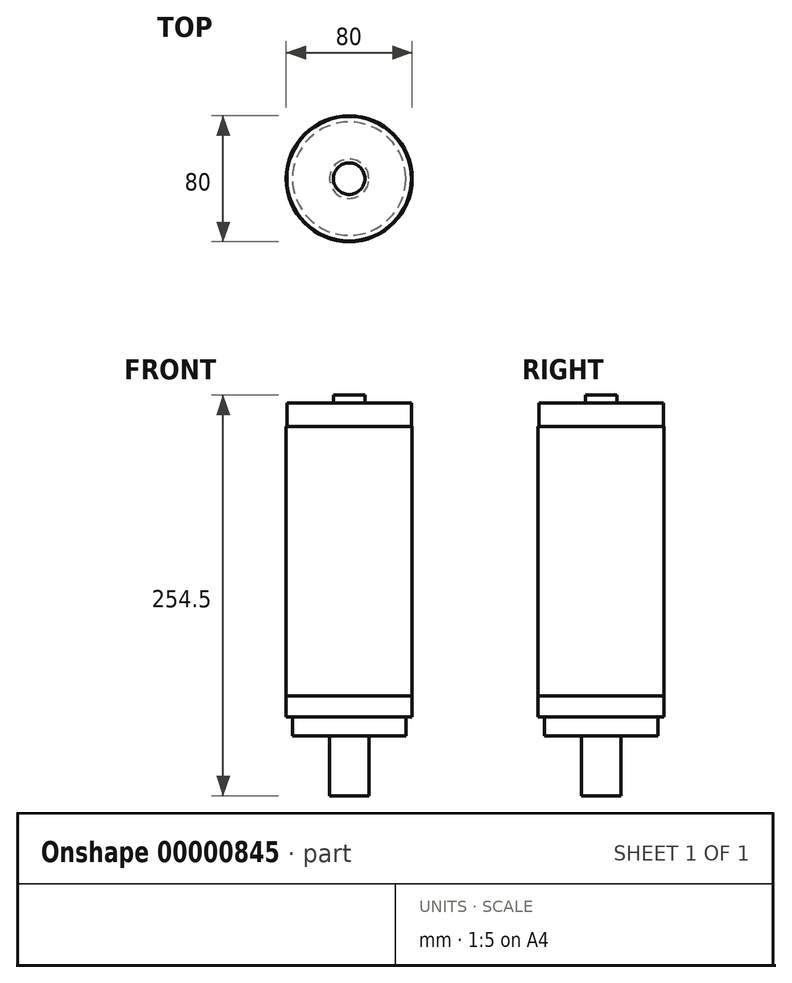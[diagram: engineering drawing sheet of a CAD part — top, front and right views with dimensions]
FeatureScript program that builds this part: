
annotation { "Feature Type Name" : "Feature", "Feature Type Description" : "" }
export const myFeature = defineFeature(function(context is Context, id is Id, definition is map)
    precondition{}
    {
        {
            var Q0;
            Q0=qCreatedBy(makeId("Top.planeOp"),FACE);
            var sketch = newSketch(context, id + "F0", { "sketchPlane" : qUnion([Q0])});
            skCircle(sketch, "E0", {"center": v(0, 0) * mm, "radius": 39.5 * mm});
            skSolve(sketch);
        }
        {
            var Q0;
            Q0=makeQuery(id+"F0.imprint","IMPRINT",FACE,{"disambiguationData":[TD([[makeQuery(id+"F0.imprint","IMPRINT",EDGE,{"derivedFrom":sQuery(id+"F0.wireOp",EDGE,"E0")}),1.0]])]});
            extrude(context, id + "F1", {"entities" : qUnion([Q0]), "oppositeDirection" : true, "depth" : 15 * mm});
        }
        {
            var Q0;
            Q0=makeQuery(id+"F1.opExtrude","CAP_FACE",FACE,{"disambiguationData":[OSD([sQuery(id+"F0.wireOp",EDGE,"E0")])],"isStart":false});
            var sketch = newSketch(context, id + "F2", { "sketchPlane" : qUnion([Q0])});
            skCircle(sketch, "E1", {"center": v(0, 0) * mm, "radius": 40 * mm});
            skSolve(sketch);
        }
        {
            var Q0;
            Q0 = qSketchRegion(id + "F2", true);
            extrude(context, id + "F3", {"entities" : qUnion([Q0]), "operationType" : NewBodyOperationType.ADD, "depth" : 171 * mm});
        }
        {
            var Q0;
            Q0=makeQuery(id+"F3.opExtrude","CAP_FACE",FACE,{"disambiguationData":[OSD([sQuery(id+"F2.wireOp",EDGE,"E1")])],"isStart":false});
            var sketch = newSketch(context, id + "F4", { "sketchPlane" : qUnion([Q0])});
            skCircle(sketch, "E2", {"center": v(0, 0) * mm, "radius": 39.95 * mm});
            skSolve(sketch);
        }
        {
            var Q0;
            Q0 = qSketchRegion(id + "F4", true);
            extrude(context, id + "F5", {"entities" : qUnion([Q0]), "operationType" : NewBodyOperationType.ADD, "depth" : 13.5 * mm});
        }
        {
            var Q0;
            Q0=makeQuery(id+"F5.opExtrude","CAP_FACE",FACE,{"disambiguationData":[OSD([sQuery(id+"F4.wireOp",EDGE,"E2")])],"isStart":false});
            var sketch = newSketch(context, id + "F6", { "sketchPlane" : qUnion([Q0])});
            skCircle(sketch, "E3", {"center": v(0, 0) * mm, "radius": 36 * mm});
            skSolve(sketch);
        }
        {
            var Q0;
            Q0 = qSketchRegion(id + "F6", true);
            extrude(context, id + "F7", {"entities" : qUnion([Q0]), "operationType" : NewBodyOperationType.ADD, "depth" : 12 * mm});
        }
        {
            var Q0;
            Q0=makeQuery(id+"F7.opExtrude","CAP_FACE",FACE,{"disambiguationData":[OSD([sQuery(id+"F6.wireOp",EDGE,"E3")])],"isStart":false});
            var sketch = newSketch(context, id + "F8", { "sketchPlane" : qUnion([Q0])});
            skCircle(sketch, "E4", {"center": v(0, 0) * mm, "radius": 12.5 * mm});
            skSolve(sketch);
        }
        {
            var Q0;
            Q0 = qSketchRegion(id + "F8", true);
            extrude(context, id + "F9", {"entities" : qUnion([Q0]), "operationType" : NewBodyOperationType.ADD, "depth" : 38 * mm});
        }
        {
            var Q0;
            Q0=makeQuery(id+"F1.opExtrude","CAP_FACE",FACE,{"disambiguationData":[OSD([sQuery(id+"F0.wireOp",EDGE,"E0")])],"isStart":true});
            var sketch = newSketch(context, id + "F10", { "sketchPlane" : qUnion([Q0])});
            skCircle(sketch, "E5", {"center": v(0, 0) * mm, "radius": 10 * mm});
            skSolve(sketch);
        }
        {
            var Q0;
            Q0 = qSketchRegion(id + "F10", true);
            extrude(context, id + "F11", {"entities" : qUnion([Q0]), "operationType" : NewBodyOperationType.ADD, "depth" : 5 * mm});
        }
    });
